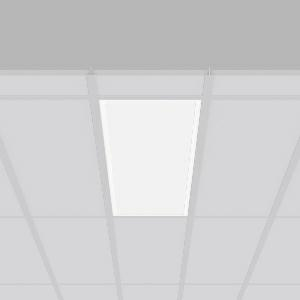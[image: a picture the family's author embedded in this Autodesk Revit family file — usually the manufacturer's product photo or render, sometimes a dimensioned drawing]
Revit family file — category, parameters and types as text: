
# Revit family: sidelite_eco_672371_002_1_07_5987
name_source: partatom
category: Lighting Fixtures
units: mm (PartAtom-declared; Revit-internal decimal feet)

## family parameters
Cut with Voids When Loaded = No
Host = Face
Light Source = No
Part Type = Normal
Room Calculation Point = No
Round Connector Dimension = Use Diameter
Shared = No

## types (1)
- SIDELITE ECO (1 x LED Modul 840, 3550 lm, 4000)
    Apparent Load = 29 VA
    CIE Flux Codes = 46 79 96 100 100
    Color Rendering = 80
    Color Temperature = 4000
    Default Elevation = 1800 mm
    Description = Series: SIDELITE ECO
Highly economical recessed luminaire with progressive LED technology. For escape route illumination. Frame made of aluminium, powder-coated. Diffuser: plastic, opal. Lightguide and diffuser made of non-yellowing plastic (PMMA). Lateral light emission (RZB SIDELITE technology) for homogeneous light distribution. External driver. Self-contained system with automatic self-test and feedback via DALI bus, only to RZB DALI monitoring system. External driver with simple plug-in locking system. Extended connection cable (1.90 m). 
Colour: white
Length: 1195 mm
Width: 295 mm
Cut-out length: 1170 mm
Cut-out width: 270 mm
Recess height: 160 mm
Luminaire: recess height: 40 mm
Weight: 4.4 kg
Operating mode: maintained power mode
Duration time: 3 h
Lamp: LED
Socket: without socket
Colour temperature: 4000K
Colour rendering index (CRI): 80
System power: 29 W
Rated luminous flux: 3550 lm
Luminous flux, emergency: 520 lm
System power, emergency: -
Control gear: Regulated power supply
Protection class: I
Type of protection: IP 40
    Height = 0 mm  [stored 0 ft]
    Lamp = 1 x LED Modul 840
    Lamp Light Flux = 3550 lm
    Lamp count = 1
    Length = 1195 mm
    Lifetime = 50000 h
    Luminous efficacy = 122 lm/W
    Manufacturer = RZB
    ModVariant = No
    Model = 672371.002.1.07
    Mounting Place = Ceiling
    Mounting Type = Recessed
    Number of Poles = 1
    OnlyDefault = Yes
    Power Factor = 1
    Product Name = SIDELITE ECO
    Product group = Recessed modular luminaires
    ProductGroupID = 406
    Protection Class = Protection class I
    Protection Degree = IP 40
    RLX_Detail_Level = 1
    RLX_Emergency_Light_Flux = 520 lm
    RLX_Emergency_Type = 3
    RLX_Emergency_Type_DB = Yes
    RlxData = <blob elided: 30749 chars, md5=2eb83cec>
    Socket = socket
    Standby Power = 0 W
    System Light Flux = 3550 lm
    System Power = 29 W
    Type Comments = Product without accessories
    Type Image = 312365.002.jpg
    URL = http://relux.com
    VarID = ---
    Voltage = 230 V
    Voltage Range = 220-240 V
    Weight = 0.00 kg
    Width = 295 mm

note: [stored X ft] marks values corroborated as IEEE doubles in the binary element streams (Revit-internal decimal feet)

## geometry (parser evidence)
native form markers: Blend x4, Sweep x12
no freeform markers — native parametric forms only
